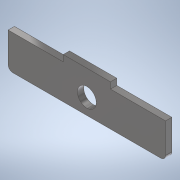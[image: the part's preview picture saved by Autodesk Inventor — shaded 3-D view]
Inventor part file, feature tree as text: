
AUTODESK INVENTOR PART (.ipt)
format: ipt  version: 2020 (Build 240168000, 168)  size: 169,984 bytes
history: native  units: mm
features: other x1, extrude x1
ambient origin geometry x8: Origin, YZ Plane, XZ Plane, XY Plane, X Axis, Y Axis, Z Axis, Center Point
bodies: Body1 (feature_tree)
feature tree (2):
  other  "實體1"
  extrude  "擠出1"  Depth=50.0mm
